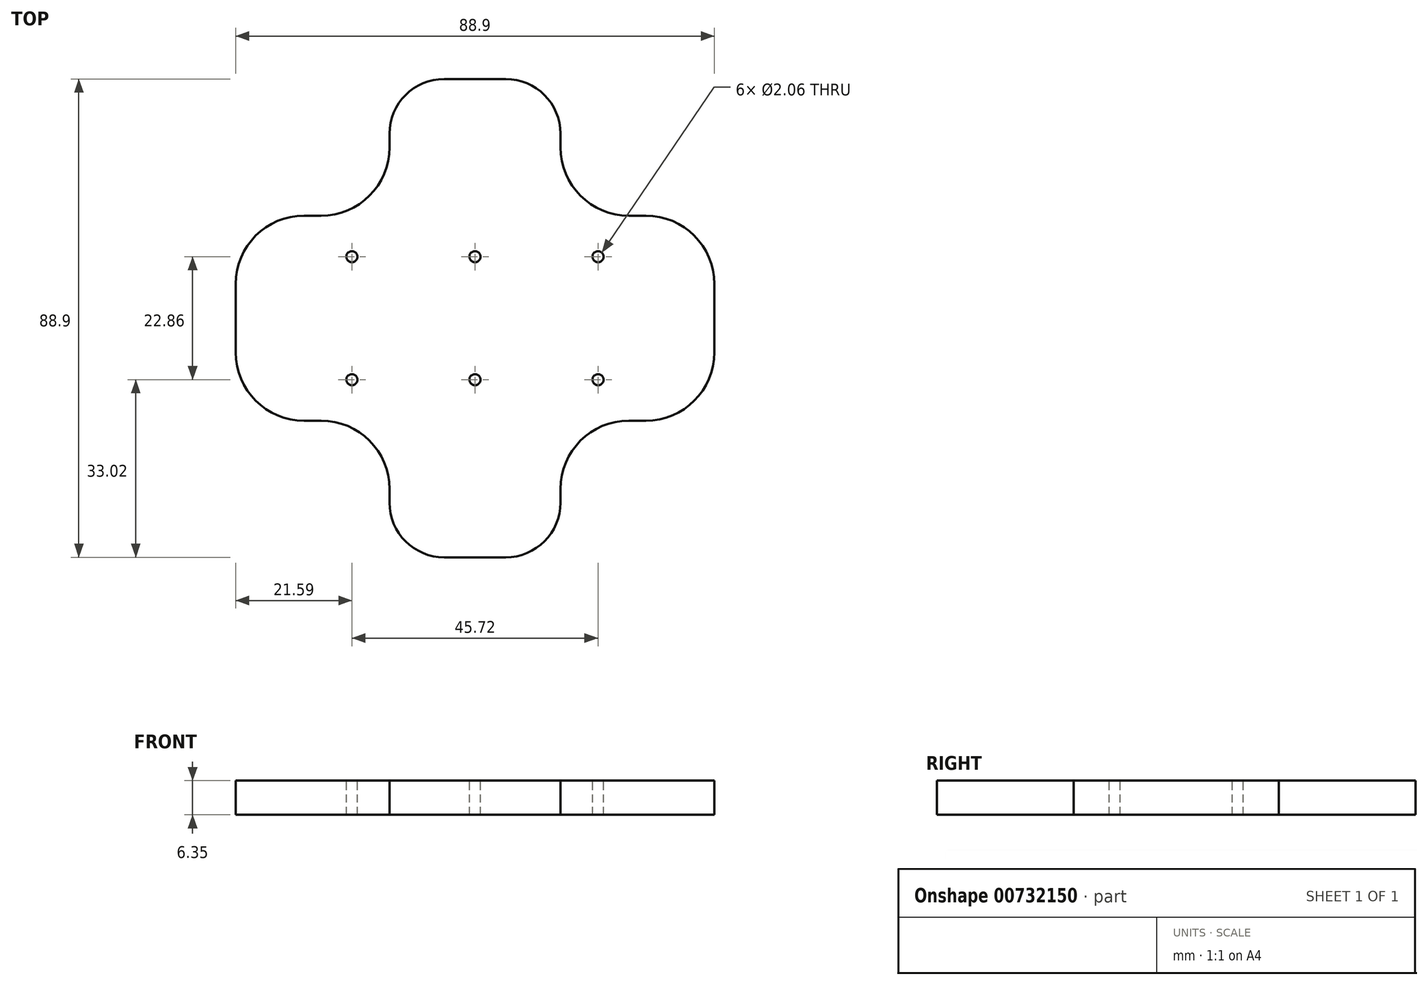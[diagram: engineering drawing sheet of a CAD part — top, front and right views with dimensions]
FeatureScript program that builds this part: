
annotation { "Feature Type Name" : "Feature", "Feature Type Description" : "" }
export const myFeature = defineFeature(function(context is Context, id is Id, definition is map)
    precondition{}
    {
        {
            var Q0;
            Q0=qCreatedBy(makeId("Top.planeOp"),FACE);
            var sketch = newSketch(context, id + "F0", { "sketchPlane" : qUnion([Q0])});
            skLineSegment(sketch, "E0.bottom", {"start": v(44.45, -19.05) * mm, "end": v(15.87, -19.05) * mm});
            skLineSegment(sketch, "E0.top", {"start": v(44.45, 19.05) * mm, "end": v(15.87, 19.05) * mm});
            skLineSegment(sketch, "E0.left", {"start": v(44.45, -19.05) * mm, "end": v(44.45, 19.05) * mm});
            skLineSegment(sketch, "E0.right", {"start": v(-44.45, -19.05) * mm, "end": v(-44.45, 19.05) * mm});
            skPoint(sketch, "E0.middle", {"position": v(0, 0) * mm});
            skLineSegment(sketch, "E1.top", {"start": v(-15.87, -44.45) * mm, "end": v(15.87, -44.45) * mm});
            skLineSegment(sketch, "E1.left", {"start": v(-15.88, -19.05) * mm, "end": v(-15.88, -44.45) * mm});
            skLineSegment(sketch, "E1.right", {"start": v(15.87, -19.05) * mm, "end": v(15.87, -44.45) * mm});
            skPoint(sketch, "E2", {"position": v(0, -44.45) * mm});
            skLineSegment(sketch, "E3.MirrorCS", {"start": v(15.88, 19.05) * mm, "end": v(15.88, 44.45) * mm});
            skLineSegment(sketch, "E4.MirrorCS", {"start": v(-15.87, 44.45) * mm, "end": v(15.87, 44.45) * mm});
            skLineSegment(sketch, "E5.MirrorCS", {"start": v(-15.87, 19.05) * mm, "end": v(-15.87, 44.45) * mm});
            skLineSegment(sketch, "E6.trimOffspring", {"start": v(-15.87, 19.05) * mm, "end": v(-44.45, 19.05) * mm});
            skLineSegment(sketch, "E7.trimOffspring", {"start": v(-15.87, -19.05) * mm, "end": v(-44.45, -19.05) * mm});
            skSolve(sketch);
        }
        {
            var Q0;
            Q0 = qSketchRegion(id + "F0", true);
            extrude(context, id + "F1", {"entities" : qUnion([Q0]), "depth" : 6.35 * mm, "offsetDistance" : 25.4 * mm});
        }
        {
            var Q0;
            Q0=makeQuery(id+"F1.opExtrude","CAP_FACE",FACE,{"disambiguationData":[OSD([sQuery(id+"F0.wireOp",EDGE,"E0.bottom"),sQuery(id+"F0.wireOp",EDGE,"E0.top"),sQuery(id+"F0.wireOp",EDGE,"E0.left"),sQuery(id+"F0.wireOp",EDGE,"E0.right"),sQuery(id+"F0.wireOp",EDGE,"E1.top"),sQuery(id+"F0.wireOp",EDGE,"E1.left"),sQuery(id+"F0.wireOp",EDGE,"E1.right"),sQuery(id+"F0.wireOp",EDGE,"E3.MirrorCS"),sQuery(id+"F0.wireOp",EDGE,"E4.MirrorCS"),sQuery(id+"F0.wireOp",EDGE,"E5.MirrorCS"),sQuery(id+"F0.wireOp",EDGE,"E6.trimOffspring"),sQuery(id+"F0.wireOp",EDGE,"E7.trimOffspring")])],"isStart":false});
            var sketch = newSketch(context, id + "F2", { "sketchPlane" : qUnion([Q0])});
            skCircle(sketch, "E8", {"center": v(-22.86, 11.43) * mm, "radius": 1.03 * mm});
            skCircle(sketch, "E9.0.1.0", {"center": v(-22.86, -11.43) * mm, "radius": 1.03 * mm});
            skCircle(sketch, "E9.1.0.0", {"center": v(0, 11.43) * mm, "radius": 1.03 * mm});
            skCircle(sketch, "E9.1.1.0", {"center": v(0, -11.43) * mm, "radius": 1.03 * mm});
            skCircle(sketch, "E9.2.0.0", {"center": v(22.86, 11.43) * mm, "radius": 1.03 * mm});
            skCircle(sketch, "E9.2.1.0", {"center": v(22.86, -11.43) * mm, "radius": 1.03 * mm});
            skLineSegment(sketch, "E9.direction1", {"start": v(-22.86, 11.43) * mm, "end": v(0, 11.43) * mm, "construction": true});
            skLineSegment(sketch, "E9.direction2", {"start": v(-22.86, 11.43) * mm, "end": v(-22.86, -11.43) * mm, "construction": true});
            skSolve(sketch);
        }
        {
            var Q0;
            Q0 = qSketchRegion(id + "F2", true);
            extrude(context, id + "F3", {"entities" : qUnion([Q0]), "operationType" : NewBodyOperationType.REMOVE, "oppositeDirection" : true, "depth" : 25.4 * mm, "offsetDistance" : 25.4 * mm});
        }
        {
            var Q0;
            Q0=makeQuery(id+"F1.opExtrude","SWEPT_EDGE",EDGE,{"disambiguationData":[OSD([sQuery(id+"F0.wireOp",EDGE,"E0.right"),sQuery(id+"F0.wireOp",EDGE,"E7.trimOffspring")])]});
            var Q1;
            Q1=makeQuery(id+"F1.opExtrude","SWEPT_EDGE",EDGE,{"disambiguationData":[OSD([sQuery(id+"F0.wireOp",EDGE,"E0.right"),sQuery(id+"F0.wireOp",EDGE,"E6.trimOffspring")])]});
            var Q2;
            Q2=makeQuery(id+"F1.opExtrude","SWEPT_EDGE",EDGE,{"disambiguationData":[OSD([sQuery(id+"F0.wireOp",EDGE,"E0.top"),sQuery(id+"F0.wireOp",EDGE,"E0.left")])]});
            var Q3;
            Q3=makeQuery(id+"F1.opExtrude","SWEPT_EDGE",EDGE,{"disambiguationData":[OSD([sQuery(id+"F0.wireOp",EDGE,"E0.bottom"),sQuery(id+"F0.wireOp",EDGE,"E0.left")])]});
            var Q4;
            Q4=makeQuery(id+"F1.opExtrude","SWEPT_EDGE",EDGE,{"disambiguationData":[OSD([sQuery(id+"F0.wireOp",EDGE,"E1.left"),sQuery(id+"F0.wireOp",EDGE,"E7.trimOffspring")])]});
            var Q5;
            Q5=makeQuery(id+"F1.opExtrude","SWEPT_EDGE",EDGE,{"disambiguationData":[OSD([sQuery(id+"F0.wireOp",EDGE,"E5.MirrorCS"),sQuery(id+"F0.wireOp",EDGE,"E6.trimOffspring")])]});
            var Q6;
            Q6=makeQuery(id+"F1.opExtrude","SWEPT_EDGE",EDGE,{"disambiguationData":[OSD([sQuery(id+"F0.wireOp",EDGE,"E0.top"),sQuery(id+"F0.wireOp",EDGE,"E3.MirrorCS")])]});
            var Q7;
            Q7=makeQuery(id+"F1.opExtrude","SWEPT_EDGE",EDGE,{"disambiguationData":[OSD([sQuery(id+"F0.wireOp",EDGE,"E0.bottom"),sQuery(id+"F0.wireOp",EDGE,"E1.right")])]});
            fillet(context, id + "F4", {"entities" : qUnion([Q0, Q1, Q2, Q3, Q4, Q5, Q6, Q7]), "radius" : 12.7 * mm, "tangentPropagation" : true, "allowEdgeOverflow" : false});
        }
        {
            var Q0;
            Q0=makeQuery(id+"F1.opExtrude","SWEPT_EDGE",EDGE,{"disambiguationData":[OSD([sQuery(id+"F0.wireOp",EDGE,"E4.MirrorCS"),sQuery(id+"F0.wireOp",EDGE,"E5.MirrorCS")])]});
            var Q1;
            Q1=makeQuery(id+"F1.opExtrude","SWEPT_EDGE",EDGE,{"disambiguationData":[OSD([sQuery(id+"F0.wireOp",EDGE,"E3.MirrorCS"),sQuery(id+"F0.wireOp",EDGE,"E4.MirrorCS")])]});
            var Q2;
            Q2=makeQuery(id+"F1.opExtrude","SWEPT_EDGE",EDGE,{"disambiguationData":[OSD([sQuery(id+"F0.wireOp",EDGE,"E1.top"),sQuery(id+"F0.wireOp",EDGE,"E1.left")])]});
            var Q3;
            Q3=makeQuery(id+"F1.opExtrude","SWEPT_EDGE",EDGE,{"disambiguationData":[OSD([sQuery(id+"F0.wireOp",EDGE,"E1.top"),sQuery(id+"F0.wireOp",EDGE,"E1.right")])]});
            fillet(context, id + "F5", {"entities" : qUnion([Q0, Q1, Q2, Q3]), "radius" : 10.16 * mm, "tangentPropagation" : true, "allowEdgeOverflow" : false});
        }
    });
